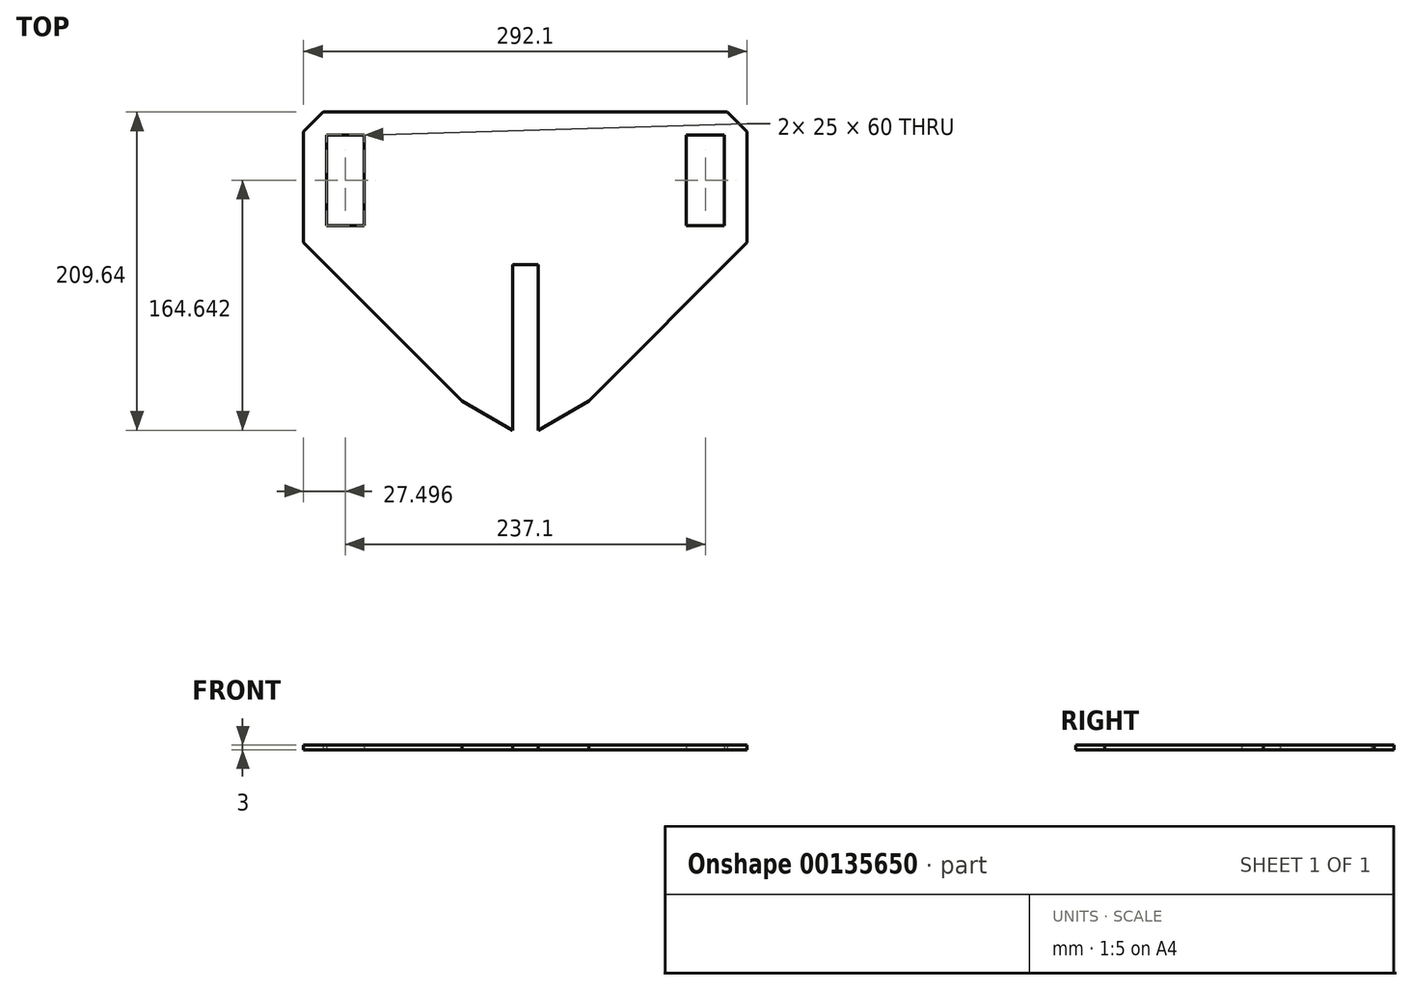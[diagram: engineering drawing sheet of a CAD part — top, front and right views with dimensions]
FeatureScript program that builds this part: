
annotation { "Feature Type Name" : "Feature", "Feature Type Description" : "" }
export const myFeature = defineFeature(function(context is Context, id is Id, definition is map)
    precondition{}
    {
        {
            var Q0;
            Q0=qCreatedBy(makeId("Top.planeOp"),FACE);
            var sketch = newSketch(context, id + "F0", { "sketchPlane" : qUnion([Q0])});
            skLineSegment(sketch, "E0", {"start": v(-133.5, 80.58) * mm, "end": v(-146.5, 67.58) * mm});
            skLineSegment(sketch, "E1", {"start": v(-146.5, 67.58) * mm, "end": v(-146.5, -5.52) * mm});
            skLineSegment(sketch, "E2", {"start": v(-146.5, -5.52) * mm, "end": v(-42.1, -109.92) * mm});
            skLineSegment(sketch, "E3", {"start": v(-8.94, -19.92) * mm, "end": v(8.06, -19.92) * mm});
            skLineSegment(sketch, "E4", {"start": v(41.2, -109.92) * mm, "end": v(145.6, -5.52) * mm});
            skLineSegment(sketch, "E5", {"start": v(145.6, -5.52) * mm, "end": v(145.6, 67.58) * mm});
            skLineSegment(sketch, "E6", {"start": v(145.6, 67.58) * mm, "end": v(132.6, 80.58) * mm});
            skLineSegment(sketch, "E7", {"start": v(132.6, 80.58) * mm, "end": v(-133.5, 80.58) * mm});
            skLineSegment(sketch, "E8.bottom", {"start": v(-131.5, 65.58) * mm, "end": v(-106.5, 65.58) * mm});
            skLineSegment(sketch, "E8.top", {"start": v(-131.5, 5.58) * mm, "end": v(-106.5, 5.58) * mm});
            skLineSegment(sketch, "E8.left", {"start": v(-131.5, 65.58) * mm, "end": v(-131.5, 5.58) * mm});
            skLineSegment(sketch, "E8.right", {"start": v(-106.5, 65.58) * mm, "end": v(-106.5, 5.58) * mm});
            skLineSegment(sketch, "E9.bottom", {"start": v(105.6, 65.58) * mm, "end": v(130.6, 65.58) * mm});
            skLineSegment(sketch, "E9.top", {"start": v(105.6, 5.58) * mm, "end": v(130.6, 5.58) * mm});
            skLineSegment(sketch, "E9.left", {"start": v(105.6, 65.58) * mm, "end": v(105.6, 5.58) * mm});
            skLineSegment(sketch, "E9.right", {"start": v(130.6, 65.58) * mm, "end": v(130.6, 5.58) * mm});
            skLineSegment(sketch, "E10", {"start": v(8.06, -19.92) * mm, "end": v(8.06, -129.06) * mm});
            skLineSegment(sketch, "E11", {"start": v(8.06, -129.06) * mm, "end": v(41.2, -109.92) * mm});
            skLineSegment(sketch, "E12", {"start": v(-8.94, -19.92) * mm, "end": v(-8.94, -129.06) * mm});
            skLineSegment(sketch, "E13", {"start": v(-8.94, -129.06) * mm, "end": v(-42.1, -109.92) * mm});
            skSolve(sketch);
        }
        {
            var Q0;
            Q0=makeQuery(id+"F0.imprint","IMPRINT",FACE,{"disambiguationData":[TD([[makeQuery(id+"F0.imprint","IMPRINT",EDGE,{"derivedFrom":sQuery(id+"F0.wireOp",EDGE,"8742dfa8-4f1c-4fec-8356-c27d79f8965c")}),1.0]])]});
            var Q1;
            Q1=makeQuery(id+"F0.imprint","IMPRINT",FACE,{"disambiguationData":[TD([[makeQuery(id+"F0.imprint","IMPRINT",EDGE,{"derivedFrom":sQuery(id+"F0.wireOp",EDGE,"34666373-eacb-403d-b7b2-1349cc378bd7")}),1.0]])]});
            var Q2;
            Q2=makeQuery(id+"F0.imprint","IMPRINT",FACE,{"disambiguationData":[TD([[makeQuery(id+"F0.imprint","IMPRINT",EDGE,{"derivedFrom":sQuery(id+"F0.wireOp",EDGE,"E0")}),1.0]])]});
            extrude(context, id + "F1", {"entities" : qUnion([Q0, Q1, Q2]), "depth" : 3 * mm});
        }
    });
